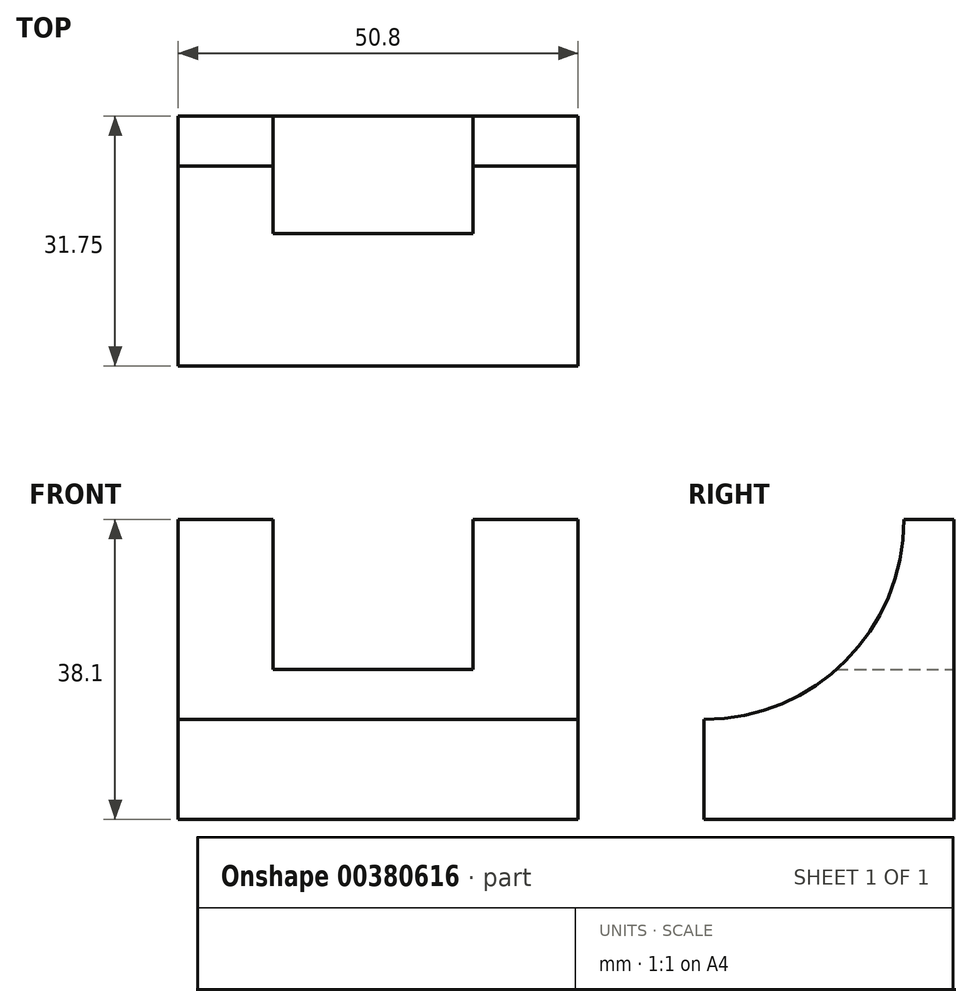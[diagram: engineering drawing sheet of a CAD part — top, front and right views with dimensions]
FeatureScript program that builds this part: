
annotation { "Feature Type Name" : "Feature", "Feature Type Description" : "" }
export const myFeature = defineFeature(function(context is Context, id is Id, definition is map)
    precondition{}
    {
        {
            var Q0;
            Q0=qCreatedBy(makeId("Front.planeOp"),FACE);
            var sketch = newSketch(context, id + "F0", { "sketchPlane" : qUnion([Q0])});
            skLineSegment(sketch, "E0.bottom", {"start": v(0, 0) * mm, "end": v(50.8, 0) * mm});
            skLineSegment(sketch, "E0.top", {"start": v(0, 38.1) * mm, "end": v(50.8, 38.1) * mm});
            skLineSegment(sketch, "E0.left", {"start": v(0, 0) * mm, "end": v(0, 38.1) * mm});
            skLineSegment(sketch, "E0.right", {"start": v(50.8, 0) * mm, "end": v(50.8, 38.1) * mm});
            skSolve(sketch);
        }
        {
            var Q0;
            Q0 = qSketchRegion(id + "F0", true);
            extrude(context, id + "F1", {"entities" : qUnion([Q0]), "depth" : 31.75 * mm});
        }
        {
            var Q0;
            Q0=makeQuery(id+"F1.opExtrude","SWEPT_FACE",FACE,{"disambiguationData":[OSD([sQuery(id+"F0.wireOp",EDGE,"E0.right")])]});
            var sketch = newSketch(context, id + "F2", { "sketchPlane" : qUnion([Q0])});
            skArc(sketch, "E1", {"start": v(-31.75, 12.7) * mm, "mid": v(-13.79, 20.14) * mm, "end": v(-6.35, 38.1) * mm});
            skSolve(sketch);
        }
        {
            var Q0;
            {var subQ0=sQuery(id+"F2.wireOp",EDGE,"E1");Q0=makeQuery(id+"F2.imprint","IMPRINT",FACE,{"disambiguationData":[TD([[makeQuery(id+"F2.imprint","IMPRINT",EDGE,{"derivedFrom":subQ0}),1.0]])]});}
            extrude(context, id + "F3", {"entities" : qUnion([Q0]), "operationType" : NewBodyOperationType.REMOVE, "oppositeDirection" : true, "depth" : 50.8 * mm});
        }
        {
            var Q0;
            Q0=makeQuery(id+"F1.opExtrude","CAP_FACE",FACE,{"disambiguationData":[OSD([sQuery(id+"F0.wireOp",EDGE,"E0.bottom"),sQuery(id+"F0.wireOp",EDGE,"E0.top"),sQuery(id+"F0.wireOp",EDGE,"E0.left"),sQuery(id+"F0.wireOp",EDGE,"E0.right")])],"isStart":true});
            var sketch = newSketch(context, id + "F4", { "sketchPlane" : qUnion([Q0])});
            skLineSegment(sketch, "E2", {"start": v(-37.45, 38.1) * mm, "end": v(-37.45, 19.05) * mm});
            skLineSegment(sketch, "E3", {"start": v(-37.45, 19.05) * mm, "end": v(-12.05, 19.05) * mm});
            skLineSegment(sketch, "E4", {"start": v(-12.05, 19.05) * mm, "end": v(-12.05, 38.1) * mm});
            skSolve(sketch);
        }
        {
            var Q0;
            {var subQ0=sQuery(id+"F4.wireOp",EDGE,"E2");Q0=makeQuery(id+"F4.imprint","IMPRINT",FACE,{"disambiguationData":[TD([[makeQuery(id+"F4.imprint","IMPRINT",EDGE,{"derivedFrom":subQ0}),1.0]])]});}
            extrude(context, id + "F5", {"entities" : qUnion([Q0]), "operationType" : NewBodyOperationType.REMOVE, "oppositeDirection" : true, "depth" : 15.62 * mm});
        }
    });
